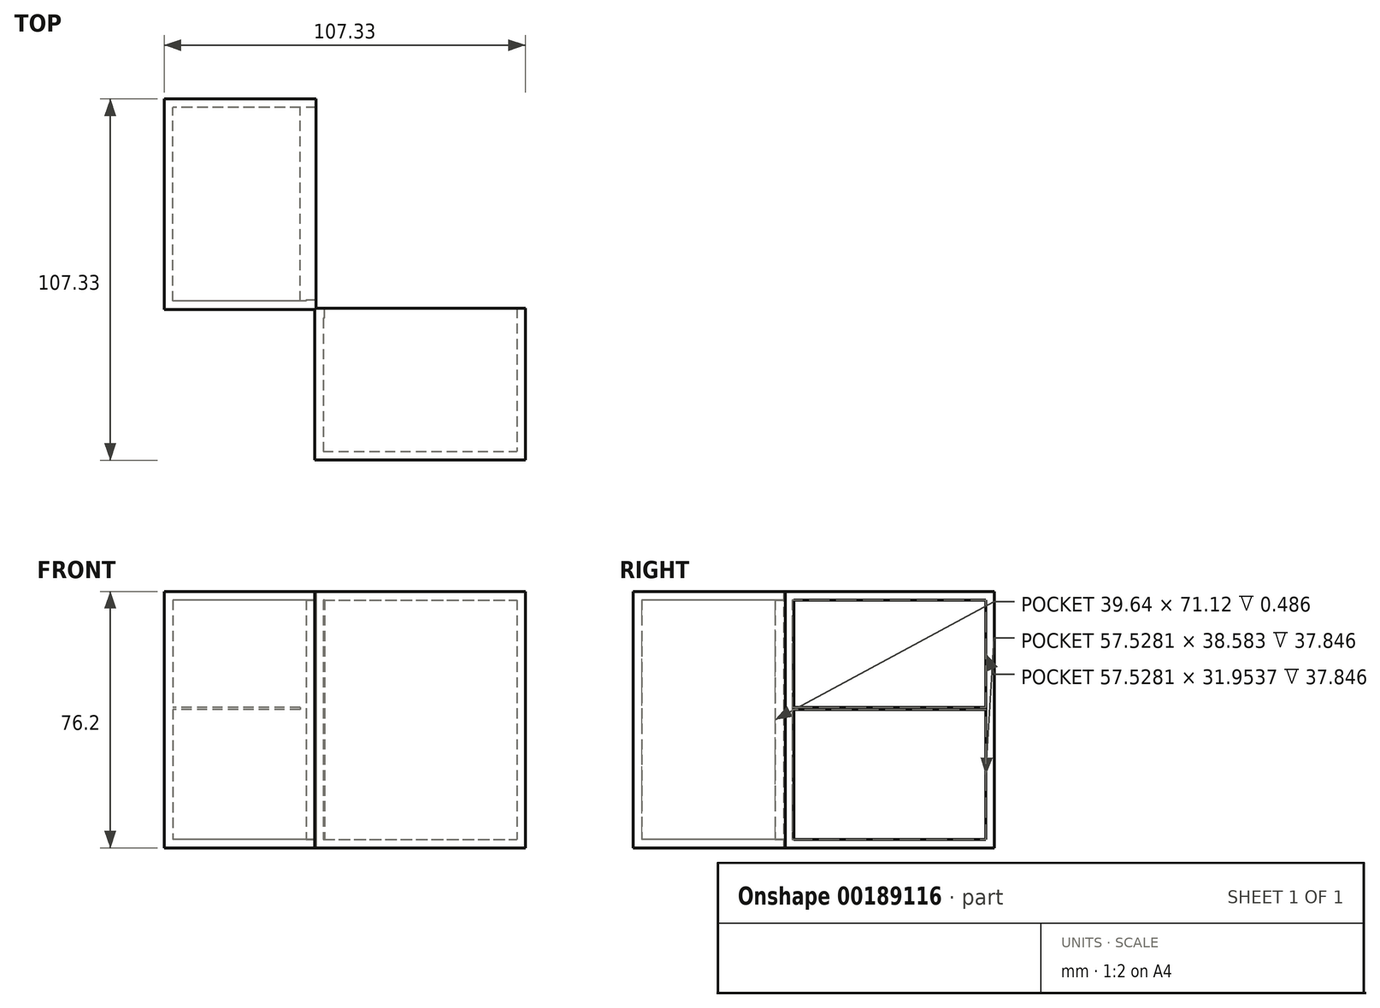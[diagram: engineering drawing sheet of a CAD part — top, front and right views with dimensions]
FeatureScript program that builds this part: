
annotation { "Feature Type Name" : "Feature", "Feature Type Description" : "" }
export const myFeature = defineFeature(function(context is Context, id is Id, definition is map)
    precondition{}
    {
        {
            var Q0;
            Q0=qCreatedBy(makeId("Top.planeOp"),FACE);
            var sketch = newSketch(context, id + "F0", { "sketchPlane" : qUnion([Q0])});
            skLineSegment(sketch, "E0.bottom", {"start": v(0, 0) * mm, "end": v(62.6, 0) * mm});
            skLineSegment(sketch, "E0.top", {"start": v(0, -45.2) * mm, "end": v(62.6, -45.2) * mm});
            skLineSegment(sketch, "E0.left", {"start": v(0, 0) * mm, "end": v(0, -45.2) * mm});
            skLineSegment(sketch, "E0.right", {"start": v(62.6, 0) * mm, "end": v(62.6, -45.2) * mm});
            skLineSegment(sketch, "E1", {"start": v(-76.22, -76.7) * mm, "end": v(76.22, 75.73) * mm});
            skLineSegment(sketch, "E2.MirrorCS", {"start": v(0.49, -0.49) * mm, "end": v(0.49, 62.12) * mm});
            skLineSegment(sketch, "E3.MirrorCS", {"start": v(0.49, -0.49) * mm, "end": v(-44.72, -0.49) * mm});
            skLineSegment(sketch, "E4.MirrorCS", {"start": v(-44.72, -0.49) * mm, "end": v(-44.72, 62.12) * mm});
            skLineSegment(sketch, "E5.MirrorCS", {"start": v(0.49, 62.12) * mm, "end": v(-44.72, 62.12) * mm});
            skSolve(sketch);
        }
        {
            var Q0;
            {var subQ0=sQuery(id+"F0.wireOp",EDGE,"E4.MirrorCS");Q0=makeQuery(id+"F0.imprint","IMPRINT",FACE,{"disambiguationData":[TD([[makeQuery(id+"F0.imprint","IMPRINT",EDGE,{"derivedFrom":subQ0}),-1.0]])]});}
            var Q1;
            {var subQ2=sQuery(id+"F0.wireOp",EDGE,"E0.top");Q1=makeQuery(id+"F0.imprint","IMPRINT",FACE,{"disambiguationData":[TD([[makeQuery(id+"F0.imprint","IMPRINT",EDGE,{"derivedFrom":subQ2}),1.0]])]});}
            extrude(context, id + "F1", {"entities" : qUnion([Q0, Q1]), "depth" : 76.2 * mm});
        }
        {
            var Q0;
            {var subQ0=sQuery(id+"F0.wireOp",EDGE,"E2.MirrorCS");Q0=makeQuery(id+"F1.opExtrude","SWEPT_FACE",FACE,{"disambiguationData":[OSD([subQ0]),TDD([makeQuery(id+"F0.imprint","IMPRINT",EDGE,{"disambiguationData":[TD([[makeQuery(id+"F0.imprint","INTERSECT",VERTEX,{"derivedFrom":[subQ0,sQuery(id+"F0.wireOp",EDGE,"E5.MirrorCS")]}),1.0]])],"derivedFrom":subQ0})])]});}
            shell(context, id + "F2", {"entities" : qUnion([Q0]), "thickness" : 2.54 * mm});
        }
        {
            var Q0;
            {var subQ0=sQuery(id+"F0.wireOp",EDGE,"E0.bottom");Q0=makeQuery(id+"F1.opExtrude","SWEPT_FACE",FACE,{"disambiguationData":[OSD([subQ0]),TDD([makeQuery(id+"F0.imprint","IMPRINT",EDGE,{"disambiguationData":[TD([[makeQuery(id+"F0.imprint","INTERSECT",VERTEX,{"derivedFrom":[subQ0,sQuery(id+"F0.wireOp",EDGE,"E0.right")]}),1.0]])],"derivedFrom":subQ0})])]});}
            shell(context, id + "F3", {"entities" : qUnion([Q0]), "thickness" : 2.54 * mm});
        }
        {
            var Q0;
            Q0=makeQuery(id+"F2.opShell","OFFSET_FACE",FACE,{"disambiguationData":[OSD([sQuery(id+"F0.wireOp",EDGE,"E4.MirrorCS")])]});
            var sketch = newSketch(context, id + "F4", { "sketchPlane" : qUnion([Q0])});
            skLineSegment(sketch, "E6.bottom", {"start": v(2.05, 41.7) * mm, "end": v(59.58, 41.7) * mm});
            skLineSegment(sketch, "E6.top", {"start": v(2.05, 41.12) * mm, "end": v(59.58, 41.12) * mm});
            skLineSegment(sketch, "E6.left", {"start": v(2.05, 41.7) * mm, "end": v(2.05, 41.12) * mm});
            skLineSegment(sketch, "E6.right", {"start": v(59.58, 41.7) * mm, "end": v(59.58, 41.12) * mm});
            skSolve(sketch);
        }
        {
            var Q0;
            Q0 = qSketchRegion(id + "F4", true);
            extrude(context, id + "F5", {"entities" : qUnion([Q0]), "operationType" : NewBodyOperationType.ADD, "depth" : 37.85 * mm});
        }
        {
            var Q0;
            Q0=makeQuery(id+"F1.opExtrude","CAP_FACE",FACE,{"disambiguationData":[OSD([sQuery(id+"F0.wireOp",EDGE,"E0.bottom"),sQuery(id+"F0.wireOp",EDGE,"E0.top"),sQuery(id+"F0.wireOp",EDGE,"E0.left"),sQuery(id+"F0.wireOp",EDGE,"E0.right"),sQuery(id+"F0.wireOp",EDGE,"E2.MirrorCS"),sQuery(id+"F0.wireOp",EDGE,"E3.MirrorCS")])],"isStart":false});
            var sketch = newSketch(context, id + "F6", { "sketchPlane" : qUnion([Q0])});
            skCircle(sketch, "E7", {"center": v(31.73, -22.6) * mm, "radius": 18.18 * mm});
            skPoint(sketch, "E7.centerSnap0", {"position": v(62.6, -22.6) * mm});
            skSolve(sketch);
        }
        {
            var Q0;
            Q0=sQuery(id+"F6.wireOp",EDGE,"E7");
            var Q1;
            Q1=makeQuery(id+"F1.opExtrude","CAP_EDGE",EDGE,{"disambiguationData":[OSD([sQuery(id+"F0.wireOp",EDGE,"E0.right")])],"isStart":false});
            revolve(context, id + "F7", {"bodyType" : ToolBodyType.SURFACE, "surfaceEntities" : qUnion([Q0]), "axis" : qUnion([Q1]), "revolveType" : RevolveType.FULL});
        }
    });
